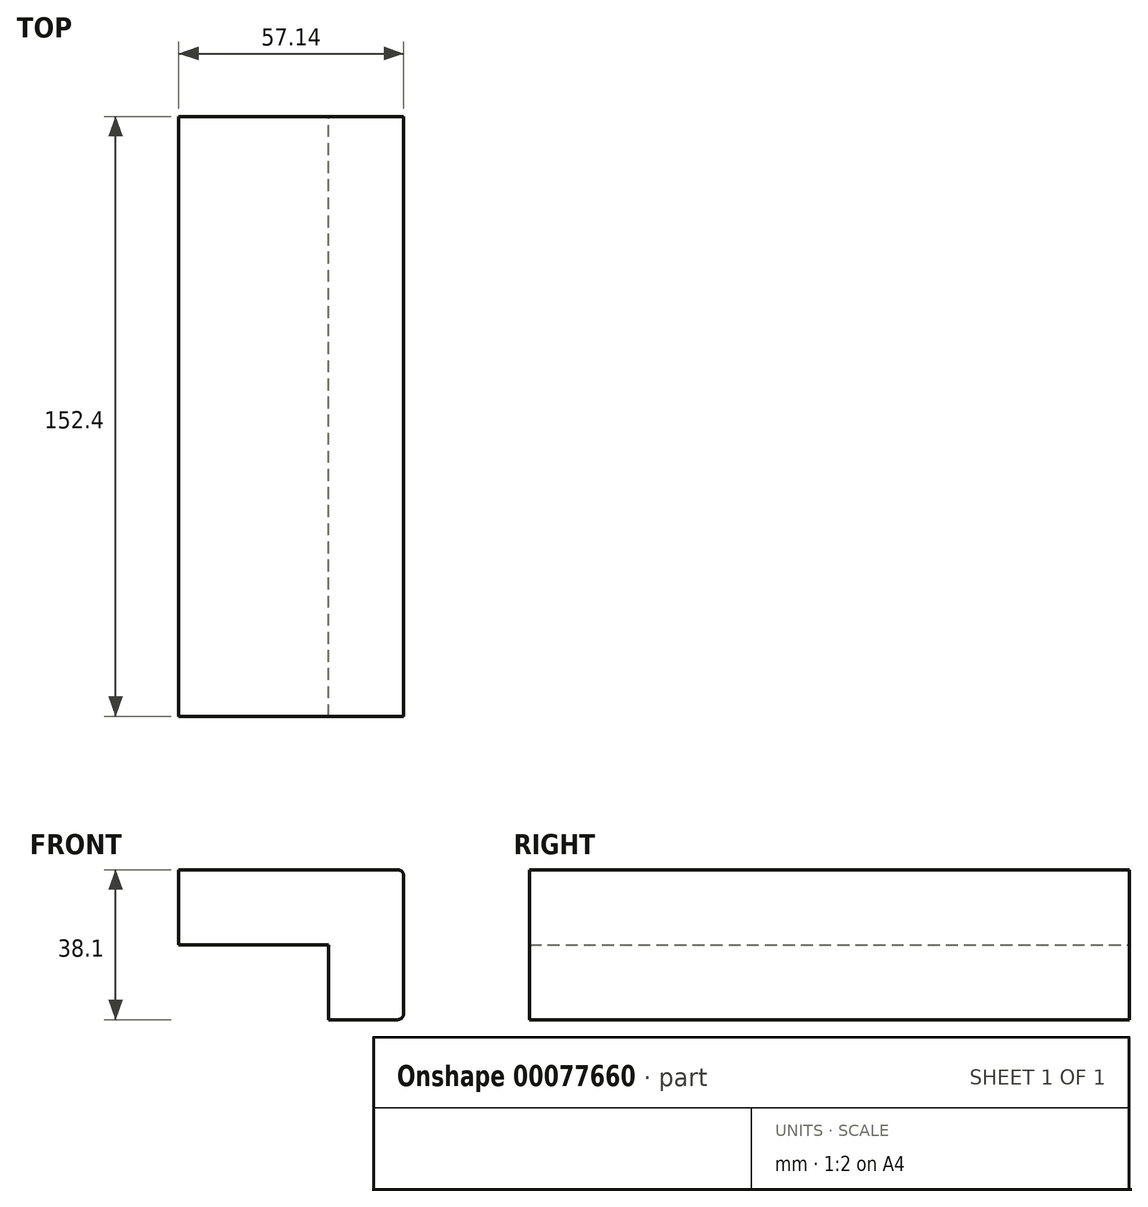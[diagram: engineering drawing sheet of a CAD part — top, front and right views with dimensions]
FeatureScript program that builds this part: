
annotation { "Feature Type Name" : "Feature", "Feature Type Description" : "" }
export const myFeature = defineFeature(function(context is Context, id is Id, definition is map)
    precondition{}
    {
        {
            var Q0;
            Q0=qCreatedBy(makeId("Front.planeOp"),FACE);
            var sketch = newSketch(context, id + "F0", { "sketchPlane" : qUnion([Q0])});
            skLineSegment(sketch, "E0", {"start": v(9.53, 19.05) * mm, "end": v(9.53, -19.05) * mm});
            skLineSegment(sketch, "E1", {"start": v(26.99, 19.05) * mm, "end": v(9.53, 19.05) * mm});
            skLineSegment(sketch, "E2", {"start": v(28.58, -17.46) * mm, "end": v(28.58, 17.46) * mm});
            skLineSegment(sketch, "E3", {"start": v(9.53, -19.05) * mm, "end": v(26.99, -19.05) * mm});
            skLineSegment(sketch, "E4", {"start": v(9.53, 19.05) * mm, "end": v(-28.58, 19.05) * mm});
            skLineSegment(sketch, "E5", {"start": v(-28.58, 19.05) * mm, "end": v(-28.58, 0) * mm});
            skLineSegment(sketch, "E6", {"start": v(-28.58, 0) * mm, "end": v(9.52, 0) * mm});
            skArc(sketch, "E7", {"start": v(26.99, -19.05) * mm, "mid": v(28.11, -18.59) * mm, "end": v(28.57, -17.46) * mm});
            skArc(sketch, "E8", {"start": v(28.57, 17.46) * mm, "mid": v(28.11, 18.59) * mm, "end": v(26.99, 19.05) * mm});
            skSolve(sketch);
        }
        {
            var Q0;
            {var subQ0=sQuery(id+"F0.wireOp",EDGE,"E4");Q0=makeQuery(id+"F0.imprint","IMPRINT",FACE,{"disambiguationData":[TD([[makeQuery(id+"F0.imprint","IMPRINT",EDGE,{"derivedFrom":subQ0}),1.0]])]});}
            var Q1;
            {var subQ1=sQuery(id+"F0.wireOp",EDGE,"E1");Q1=makeQuery(id+"F0.imprint","IMPRINT",FACE,{"disambiguationData":[TD([[makeQuery(id+"F0.imprint","IMPRINT",EDGE,{"derivedFrom":subQ1}),1.0]])]});}
            extrude(context, id + "F1", {"entities" : qUnion([Q0, Q1]), "depth" : 152.4 * mm});
        }
    });
